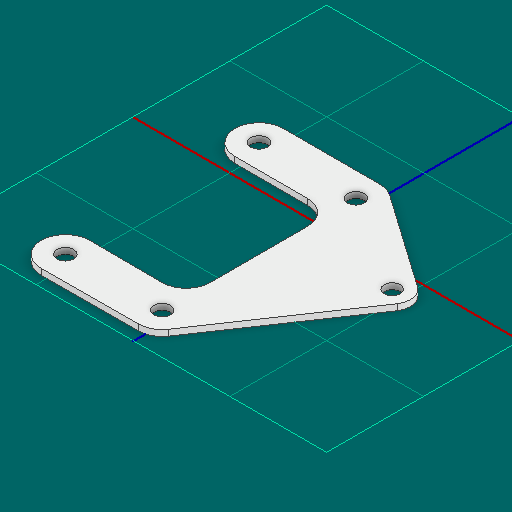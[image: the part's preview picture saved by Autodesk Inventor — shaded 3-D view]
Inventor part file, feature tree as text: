
AUTODESK INVENTOR PART (.ipt)
format: ipt  version: 2025 (Build 290162000, 162)  size: 133,120 bytes
history: native  units: in
note: dims shown in document units (in); Inventor stores cm internally (conversion verified against a paired STEP export)
features: extrude x1, sketch x1
ambient origin geometry x8: Origin, YZ Plane, XZ Plane, XY Plane, X Axis, Y Axis, Z Axis, Center Point
bodies: Solid1 (feature_tree)
feature tree (2):
  extrude  "Extrusion1"  Depth=0.0625in TaperAngle=0.0deg
  sketch  "Sketch1"  dims[d0=0.165in d1=0.375in d2=1.0in d3=0.25in d4=0.0625in d5=0.0in]
